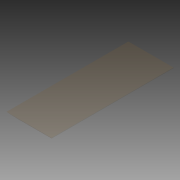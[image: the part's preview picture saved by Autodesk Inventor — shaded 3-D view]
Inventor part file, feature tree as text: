
AUTODESK INVENTOR PART (.ipt)
format: ipt  version: 2012 (Build 160160000, 160)  size: 67,584 bytes
history: native  units: in
note: dims shown in document units (in); Inventor stores cm internally (conversion verified against a paired STEP export)
features: extrude x1, sketch x1
ambient origin geometry x8: Origin, YZ Plane, XZ Plane, XY Plane, X Axis, Y Axis, Z Axis, Center Point
bodies: Solid1 (feature_tree)
feature tree (2):
  extrude  "Extrusion1"  Depth=0.125in
  sketch  "Sketch1"  dims[d1=10.0in d2=0.125in d3=0.0216in d4=27.0in d5=0.0in]
